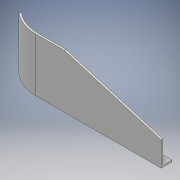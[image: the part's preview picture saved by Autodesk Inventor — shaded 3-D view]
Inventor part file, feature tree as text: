
AUTODESK INVENTOR PART (.ipt)
format: ipt  version: 2018 (Build 220112000, 112)  size: 176,640 bytes
history: native  units: mm
features: extrude x7, sketch x7, other x1
ambient origin geometry x8: Origin, YZ Plane, XZ Plane, XY Plane, X Axis, Y Axis, Z Axis, Center Point
bodies: Body1 (feature_tree)
feature tree (15):
  extrude  "押し出し1"  Depth=250.0mm
  extrude  "押し出し2"  Depth=500.0mm
  extrude  "押し出し5"  Depth=100.0mm
  extrude  "押し出し7"  Depth=200.0mm
  other  "面を削除1"
  extrude  "押し出し9"  Depth=35.0mm TaperAngle=0.0deg
  extrude  "押し出し10"  Depth=90.0mm
  extrude  "押し出し11"  Depth=35.0mm TaperAngle=0.0deg
  sketch  "スケッチ1"
  sketch  "スケッチ2"
  sketch  "スケッチ5"
  sketch  "スケッチ8"
  sketch  "スケッチ10"
  sketch  "スケッチ11"
  sketch  "スケッチ12"
